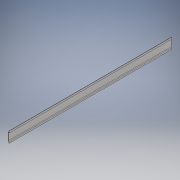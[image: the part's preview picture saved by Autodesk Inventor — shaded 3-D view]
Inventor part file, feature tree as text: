
AUTODESK INVENTOR PART (.ipt)
format: ipt  version: 2018 (Build 220112000, 112)  size: 123,392 bytes
history: native  units: mm
features: extrude x1, sketch x1
ambient origin geometry x8: Origin, YZ Plane, XZ Plane, XY Plane, X Axis, Y Axis, Z Axis, Center Point
bodies: Volumenkörper1 (feature_tree)
feature tree (2):
  extrude  "Extrusion1"  Depth=13.0mm
  sketch  "Skizze1"  dims[d0=1.15mm d1=13.0mm d2=0.3mm d3=0.3mm d4=9.3mm d7=75.0deg d8=0.3mm d9=0.3mm d10=75.0deg d11=0.3mm d12=0.3mm d13=200.0mm d14=0.0mm]
